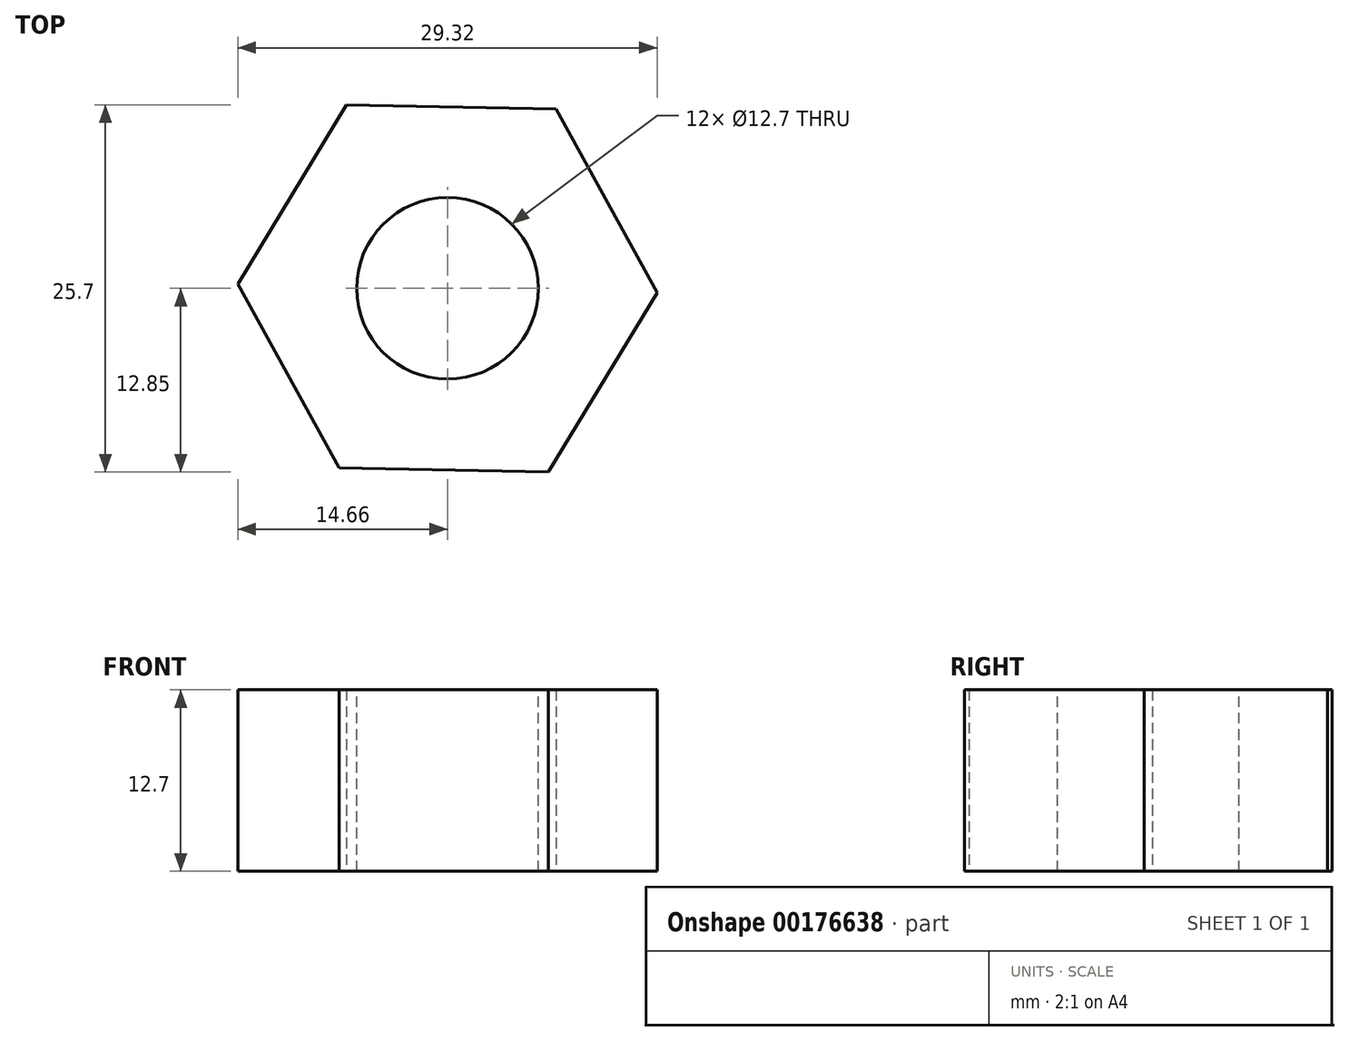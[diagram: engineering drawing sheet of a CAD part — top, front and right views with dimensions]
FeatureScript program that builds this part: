
annotation { "Feature Type Name" : "Feature", "Feature Type Description" : "" }
export const myFeature = defineFeature(function(context is Context, id is Id, definition is map)
    precondition{}
    {
        {
            var Q0;
            Q0=qCreatedBy(makeId("Top.planeOp"),FACE);
            var sketch = newSketch(context, id + "F0", { "sketchPlane" : qUnion([Q0])});
            skCircle(sketch, "E0.cCircle", {"center": v(0, 0) * mm, "radius": 12.7 * mm, "construction": true});
            skLineSegment(sketch, "E0.0", {"start": v(7.59, 12.55) * mm, "end": v(14.66, -0.3) * mm});
            skLineSegment(sketch, "E0.1", {"start": v(14.66, -0.3) * mm, "end": v(7.07, -12.85) * mm});
            skLineSegment(sketch, "E0.2", {"start": v(7.07, -12.85) * mm, "end": v(-7.59, -12.55) * mm});
            skLineSegment(sketch, "E0.3", {"start": v(-7.59, -12.55) * mm, "end": v(-14.66, 0.3) * mm});
            skLineSegment(sketch, "E0.4", {"start": v(-14.66, 0.3) * mm, "end": v(-7.07, 12.85) * mm});
            skLineSegment(sketch, "E0.5", {"start": v(-7.07, 12.85) * mm, "end": v(7.59, 12.55) * mm});
            skPoint(sketch, "E0.0.midPoint", {"position": v(11.13, 6.12) * mm});
            skSolve(sketch);
        }
        {
            var Q0;
            Q0=makeQuery(id+"F0.imprint","IMPRINT",FACE,{"disambiguationData":[TD([[makeQuery(id+"F0.imprint","IMPRINT",EDGE,{"derivedFrom":sQuery(id+"F0.wireOp",EDGE,"E0.0")}),-1.0]])]});
            extrude(context, id + "F1", {"entities" : qUnion([Q0]), "depth" : 12.7 * mm});
        }
        {
            var Q0;
            Q0=makeQuery(id+"F1.opExtrude","CAP_FACE",FACE,{"disambiguationData":[OSD([sQuery(id+"F0.wireOp",EDGE,"E0.0"),sQuery(id+"F0.wireOp",EDGE,"E0.1"),sQuery(id+"F0.wireOp",EDGE,"E0.2"),sQuery(id+"F0.wireOp",EDGE,"E0.3"),sQuery(id+"F0.wireOp",EDGE,"E0.4"),sQuery(id+"F0.wireOp",EDGE,"E0.5")])],"isStart":false});
            var sketch = newSketch(context, id + "F2", { "sketchPlane" : qUnion([Q0])});
            skCircle(sketch, "E1", {"center": v(0, 0) * mm, "radius": 6.35 * mm});
            skSolve(sketch);
        }
        {
            var Q0;
            Q0=makeQuery(id+"F2.imprint","IMPRINT",FACE,{"disambiguationData":[TD([[makeQuery(id+"F2.imprint","IMPRINT",EDGE,{"derivedFrom":sQuery(id+"F2.wireOp",EDGE,"E1")}),1.0]])]});
            extrude(context, id + "F3", {"entities" : qUnion([Q0]), "operationType" : NewBodyOperationType.REMOVE, "endBound" : BoundingType.THROUGH_ALL, "oppositeDirection" : true, "depth" : 25.4 * mm});
        }
    });
